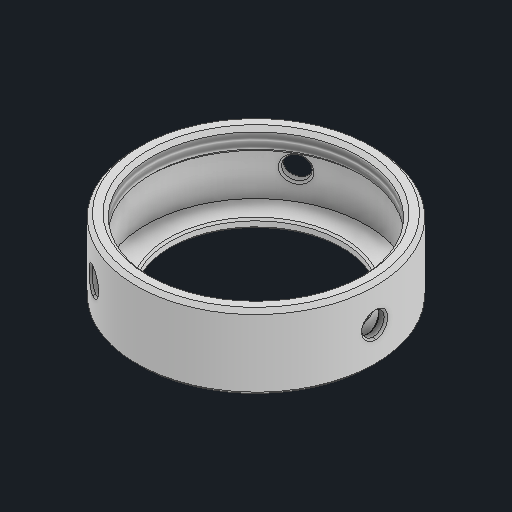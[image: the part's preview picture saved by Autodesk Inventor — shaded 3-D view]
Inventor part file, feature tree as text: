
AUTODESK INVENTOR PART (.ipt)
format: ipt  version: 2022 (Build 260153000, 153)  size: 253,952 bytes
history: native  units: mm
features: chamfer x4, sketch x2, revolve x1, thread x1, plane x1, hole x1, pattern_circular x1
ambient origin geometry x8: Origin, YZ Plane, XZ Plane, XY Plane, X Axis, Y Axis, Z Axis, Center Point
bodies: Solid1 (feature_tree)
feature tree (11):
  revolve  "Revolution1"  [1 undecoded]
  chamfer  "Chamfer1"  Distance=2.0mm
  thread  "Thread1"  [1 undecoded]
  chamfer  "Chamfer2"  Distance=3.0mm
  chamfer  "Chamfer3"  Distance=10.0mm
  plane  "Work Plane1"
  hole  "Hole1"  [1 undecoded]
  chamfer  "Chamfer4"  Distance=0.5mm
  pattern_circular  "Circular Pattern1"  [2 undecoded]
  sketch  "Sketch1"  dims[d0=23.0mm d1=1.2mm]
  sketch  "Sketch2"  dims[d2=1.2mm d3=2.0mm d4=32.0mm d5=3.0mm d6=10.0mm d7=90.0deg d8=0.5mm d9=0.5mm d10=0.5mm d11=2.0mm d12=45.0deg d13=3.0mm d14=0.0mm d15=0.25mm d16=2.0mm d17=45.0deg d18=0.5mm d19=2.0mm d20=45.0deg d21=3.0mm d22=5.0mm d23=4.0mm d24=2.0mm d25=90.0deg d26=5.0mm d27=0.0mm d28=0.25mm d29=2.0mm d30=45.0deg d31=30.0mm d32=360.0deg]
note: 5 required parameter values undecoded (feature->parameter linkage not recoverable at this tier; creation-order binding heuristic only, values carry confidence <= 0.55)